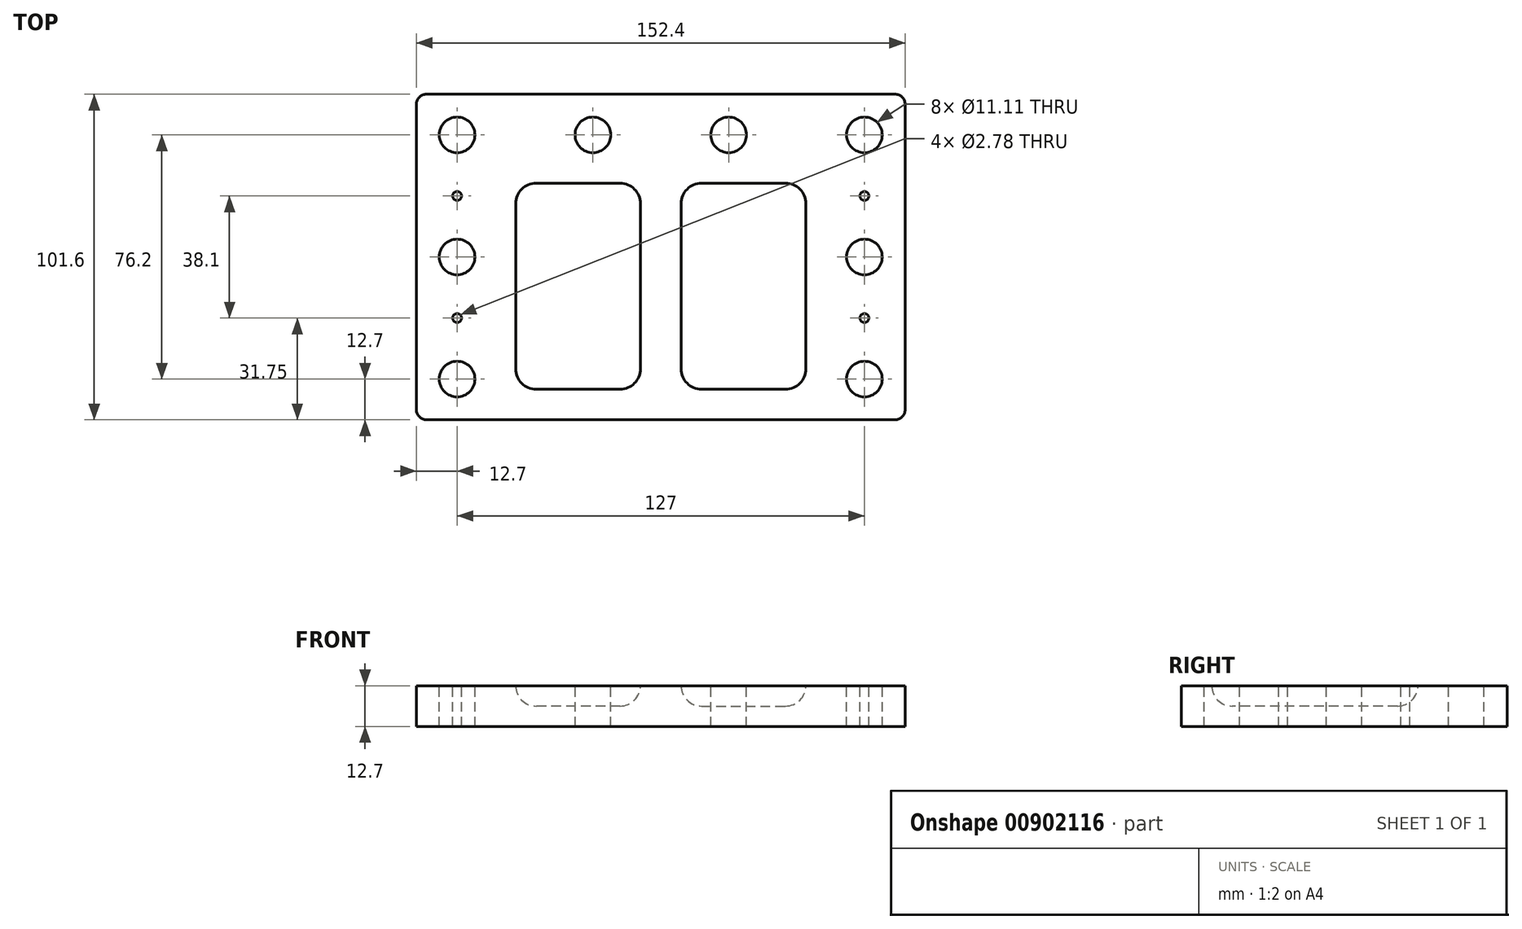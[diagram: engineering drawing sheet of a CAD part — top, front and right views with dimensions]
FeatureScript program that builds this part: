
annotation { "Feature Type Name" : "Feature", "Feature Type Description" : "" }
export const myFeature = defineFeature(function(context is Context, id is Id, definition is map)
    precondition{}
    {
        {
            var Q0;
            Q0=qCreatedBy(makeId("Top.planeOp"),FACE);
            var sketch = newSketch(context, id + "F0", { "sketchPlane" : qUnion([Q0])});
            skLineSegment(sketch, "E0.bottom", {"start": v(73.03, -50.8) * mm, "end": v(-73.02, -50.8) * mm});
            skLineSegment(sketch, "E0.top", {"start": v(73.03, 50.8) * mm, "end": v(-73.02, 50.8) * mm});
            skLineSegment(sketch, "E0.left", {"start": v(76.2, -47.63) * mm, "end": v(76.2, 47.63) * mm});
            skLineSegment(sketch, "E0.right", {"start": v(-76.2, -47.63) * mm, "end": v(-76.2, 47.63) * mm});
            skPoint(sketch, "E0.middle", {"position": v(0, 0) * mm});
            skPoint(sketch, "E1.visualSharp", {"position": v(76.2, -50.8) * mm});
            skArc(sketch, "E1.filletArc", {"start": v(73.03, -50.8) * mm, "mid": v(75.27, -49.87) * mm, "end": v(76.2, -47.63) * mm});
            skPoint(sketch, "E2.visualSharp", {"position": v(76.2, 50.8) * mm});
            skArc(sketch, "E2.filletArc", {"start": v(76.2, 47.63) * mm, "mid": v(75.27, 49.87) * mm, "end": v(73.03, 50.8) * mm});
            skPoint(sketch, "E3.visualSharp", {"position": v(-76.2, 50.8) * mm});
            skArc(sketch, "E3.filletArc", {"start": v(-73.02, 50.8) * mm, "mid": v(-75.27, 49.87) * mm, "end": v(-76.2, 47.63) * mm});
            skPoint(sketch, "E4.visualSharp", {"position": v(-76.2, -50.8) * mm});
            skArc(sketch, "E4.filletArc", {"start": v(-76.2, -47.63) * mm, "mid": v(-75.27, -49.87) * mm, "end": v(-73.02, -50.8) * mm});
            skSolve(sketch);
        }
        {
            var Q0;
            Q0 = qSketchRegion(id + "F0", true);
            extrude(context, id + "F1", {"entities" : qUnion([Q0]), "depth" : 12.7 * mm, "offsetDistance" : 25.4 * mm});
        }
        {
            var Q0;
            Q0=makeQuery(id+"F1.opExtrude","CAP_FACE",FACE,{"disambiguationData":[OSD([sQuery(id+"F0.wireOp",EDGE,"E0.bottom"),sQuery(id+"F0.wireOp",EDGE,"E0.top"),sQuery(id+"F0.wireOp",EDGE,"E0.left"),sQuery(id+"F0.wireOp",EDGE,"E0.right"),sQuery(id+"F0.wireOp",EDGE,"E1.filletArc"),sQuery(id+"F0.wireOp",EDGE,"E2.filletArc"),sQuery(id+"F0.wireOp",EDGE,"E3.filletArc"),sQuery(id+"F0.wireOp",EDGE,"E4.filletArc")])],"isStart":false});
            var sketch = newSketch(context, id + "F2", { "sketchPlane" : qUnion([Q0])});
            skCircle(sketch, "E5", {"center": v(-63.5, -19.05) * mm, "radius": 1.39 * mm});
            skCircle(sketch, "E6", {"center": v(63.5, 19.05) * mm, "radius": 1.39 * mm});
            skCircle(sketch, "E7", {"center": v(63.5, -19.05) * mm, "radius": 1.39 * mm});
            skCircle(sketch, "E8", {"center": v(-63.5, 19.05) * mm, "radius": 1.39 * mm});
            skLineSegment(sketch, "E9", {"start": v(-63.5, 19.05) * mm, "end": v(63.5, -19.05) * mm, "construction": true});
            skLineSegment(sketch, "E10", {"start": v(-63.5, -19.05) * mm, "end": v(63.5, 19.05) * mm, "construction": true});
            skSolve(sketch);
        }
        {
            var Q0;
            Q0=makeQuery(id+"F1.opExtrude","CAP_FACE",FACE,{"disambiguationData":[OSD([sQuery(id+"F0.wireOp",EDGE,"E0.bottom"),sQuery(id+"F0.wireOp",EDGE,"E0.top"),sQuery(id+"F0.wireOp",EDGE,"E0.left"),sQuery(id+"F0.wireOp",EDGE,"E0.right"),sQuery(id+"F0.wireOp",EDGE,"E1.filletArc"),sQuery(id+"F0.wireOp",EDGE,"E2.filletArc"),sQuery(id+"F0.wireOp",EDGE,"E3.filletArc"),sQuery(id+"F0.wireOp",EDGE,"E4.filletArc")])],"isStart":false});
            var sketch = newSketch(context, id + "F3", { "sketchPlane" : qUnion([Q0])});
            skCircle(sketch, "E11", {"center": v(-63.5, 38.1) * mm, "radius": 5.56 * mm});
            skCircle(sketch, "E12", {"center": v(63.5, 38.1) * mm, "radius": 5.56 * mm});
            skCircle(sketch, "E13", {"center": v(63.5, -38.1) * mm, "radius": 5.56 * mm});
            skCircle(sketch, "E14", {"center": v(-63.5, -38.1) * mm, "radius": 5.56 * mm});
            skCircle(sketch, "E15", {"center": v(-63.5, 0) * mm, "radius": 5.56 * mm});
            skCircle(sketch, "E16", {"center": v(63.5, 0) * mm, "radius": 5.56 * mm});
            skCircle(sketch, "E17", {"center": v(-21.17, 38.1) * mm, "radius": 5.56 * mm});
            skCircle(sketch, "E18", {"center": v(21.17, 38.1) * mm, "radius": 5.56 * mm});
            skLineSegment(sketch, "E19", {"start": v(-63.5, 38.1) * mm, "end": v(-63.5, 0) * mm, "construction": true});
            skLineSegment(sketch, "E20", {"start": v(-63.5, 0) * mm, "end": v(-63.5, -38.1) * mm, "construction": true});
            skLineSegment(sketch, "E21", {"start": v(63.5, 38.1) * mm, "end": v(21.17, 38.1) * mm, "construction": true});
            skLineSegment(sketch, "E22", {"start": v(-63.5, 38.1) * mm, "end": v(-21.17, 38.1) * mm, "construction": true});
            skLineSegment(sketch, "E23", {"start": v(-21.17, 38.1) * mm, "end": v(21.17, 38.1) * mm, "construction": true});
            skSolve(sketch);
        }
        {
            var Q0;
            Q0 = qSketchRegion(id + "F3", true);
            extrude(context, id + "F4", {"entities" : qUnion([Q0]), "operationType" : NewBodyOperationType.REMOVE, "endBound" : BoundingType.THROUGH_ALL, "oppositeDirection" : true, "depth" : 25.4 * mm, "offsetDistance" : 25.4 * mm});
        }
        {
            var Q0;
            Q0 = qSketchRegion(id + "F2", true);
            extrude(context, id + "F5", {"entities" : qUnion([Q0]), "operationType" : NewBodyOperationType.REMOVE, "endBound" : BoundingType.THROUGH_ALL, "oppositeDirection" : true, "depth" : 25.4 * mm, "offsetDistance" : 25.4 * mm});
        }
        {
            var Q0;
            Q0=makeQuery(id+"F1.opExtrude","CAP_FACE",FACE,{"disambiguationData":[OSD([sQuery(id+"F0.wireOp",EDGE,"E0.bottom"),sQuery(id+"F0.wireOp",EDGE,"E0.top"),sQuery(id+"F0.wireOp",EDGE,"E0.left"),sQuery(id+"F0.wireOp",EDGE,"E0.right"),sQuery(id+"F0.wireOp",EDGE,"E1.filletArc"),sQuery(id+"F0.wireOp",EDGE,"E2.filletArc"),sQuery(id+"F0.wireOp",EDGE,"E3.filletArc"),sQuery(id+"F0.wireOp",EDGE,"E4.filletArc")])],"isStart":false});
            var sketch = newSketch(context, id + "F6", { "sketchPlane" : qUnion([Q0])});
            skLineSegment(sketch, "E24.bottom", {"start": v(-12.7, 23.02) * mm, "end": v(-38.9, 23.02) * mm});
            skLineSegment(sketch, "E24.top", {"start": v(-12.7, -41.28) * mm, "end": v(-38.9, -41.28) * mm});
            skLineSegment(sketch, "E24.left", {"start": v(-6.35, 16.67) * mm, "end": v(-6.35, -34.93) * mm});
            skLineSegment(sketch, "E24.right", {"start": v(-45.24, 16.67) * mm, "end": v(-45.24, -34.93) * mm});
            skPoint(sketch, "E24.middle", {"position": v(-25.8, -9.13) * mm});
            skPoint(sketch, "E25.visualSharp", {"position": v(-6.35, 23.02) * mm});
            skArc(sketch, "E25.filletArc", {"start": v(-6.35, 16.67) * mm, "mid": v(-8.2, 21.16) * mm, "end": v(-12.7, 23.02) * mm});
            skPoint(sketch, "E26.visualSharp", {"position": v(-45.24, 23.02) * mm});
            skArc(sketch, "E26.filletArc", {"start": v(-38.9, 23.02) * mm, "mid": v(-43.38, 21.16) * mm, "end": v(-45.24, 16.67) * mm});
            skPoint(sketch, "E27.visualSharp", {"position": v(-45.24, -41.28) * mm});
            skArc(sketch, "E27.filletArc", {"start": v(-45.24, -34.93) * mm, "mid": v(-43.38, -39.42) * mm, "end": v(-38.9, -41.28) * mm});
            skPoint(sketch, "E28.visualSharp", {"position": v(-6.35, -41.28) * mm});
            skArc(sketch, "E28.filletArc", {"start": v(-12.7, -41.28) * mm, "mid": v(-8.2, -39.42) * mm, "end": v(-6.35, -34.93) * mm});
            skArc(sketch, "E29.MirrorCS", {"start": v(12.7, -41.28) * mm, "mid": v(8.2, -39.42) * mm, "end": v(6.35, -34.93) * mm});
            skArc(sketch, "E30.MirrorCS", {"start": v(45.24, -34.93) * mm, "mid": v(43.38, -39.42) * mm, "end": v(38.9, -41.28) * mm});
            skArc(sketch, "E31.MirrorCS", {"start": v(38.9, 23.02) * mm, "mid": v(43.38, 21.16) * mm, "end": v(45.24, 16.67) * mm});
            skArc(sketch, "E32.MirrorCS", {"start": v(6.35, 16.67) * mm, "mid": v(8.2, 21.16) * mm, "end": v(12.7, 23.02) * mm});
            skLineSegment(sketch, "E33.MirrorCS", {"start": v(45.24, 16.67) * mm, "end": v(45.24, -34.93) * mm});
            skPoint(sketch, "E34.MirrorP", {"position": v(6.35, 23.02) * mm});
            skPoint(sketch, "E35.MirrorP", {"position": v(25.8, -9.13) * mm});
            skLineSegment(sketch, "E36.MirrorCS", {"start": v(12.7, 23.02) * mm, "end": v(38.9, 23.02) * mm});
            skPoint(sketch, "E37.MirrorP", {"position": v(45.24, -41.28) * mm});
            skPoint(sketch, "E38.MirrorP", {"position": v(6.35, -41.28) * mm});
            skPoint(sketch, "E39.MirrorP", {"position": v(45.24, 23.02) * mm});
            skLineSegment(sketch, "E40.MirrorCS", {"start": v(6.35, 16.67) * mm, "end": v(6.35, -34.93) * mm});
            skLineSegment(sketch, "E41.MirrorCS", {"start": v(12.7, -41.28) * mm, "end": v(38.9, -41.28) * mm});
            skSolve(sketch);
        }
        {
            var Q0;
            Q0 = qSketchRegion(id + "F6", true);
            extrude(context, id + "F7", {"entities" : qUnion([Q0]), "operationType" : NewBodyOperationType.REMOVE, "oppositeDirection" : true, "depth" : 6.35 * mm, "offsetDistance" : 25.4 * mm});
        }
        {
            var Q0;
            Q0=makeQuery(id+"F7.boolean.opBoolean","COPY",EDGE,{"derivedFrom":makeQuery(id+"F7.opExtrude","CAP_EDGE",EDGE,{"disambiguationData":[OSD([sQuery(id+"F6.wireOp",EDGE,"E24.top")])],"isStart":false})});
            var Q1;
            Q1=makeQuery(id+"F7.boolean.opBoolean","COPY",EDGE,{"derivedFrom":makeQuery(id+"F7.opExtrude","CAP_EDGE",EDGE,{"disambiguationData":[OSD([sQuery(id+"F6.wireOp",EDGE,"E24.left")])],"isStart":false})});
            var Q2;
            Q2=makeQuery(id+"F7.boolean.opBoolean","COPY",EDGE,{"derivedFrom":makeQuery(id+"F7.opExtrude","CAP_EDGE",EDGE,{"disambiguationData":[OSD([sQuery(id+"F6.wireOp",EDGE,"E28.filletArc")])],"isStart":false})});
            var Q3;
            Q3=makeQuery(id+"F7.boolean.opBoolean","COPY",EDGE,{"derivedFrom":makeQuery(id+"F7.opExtrude","CAP_EDGE",EDGE,{"disambiguationData":[OSD([sQuery(id+"F6.wireOp",EDGE,"E24.right")])],"isStart":false})});
            var Q4;
            Q4=makeQuery(id+"F7.boolean.opBoolean","COPY",EDGE,{"derivedFrom":makeQuery(id+"F7.opExtrude","CAP_EDGE",EDGE,{"disambiguationData":[OSD([sQuery(id+"F6.wireOp",EDGE,"E27.filletArc")])],"isStart":false})});
            var Q5;
            Q5=makeQuery(id+"F7.boolean.opBoolean","COPY",EDGE,{"derivedFrom":makeQuery(id+"F7.opExtrude","CAP_EDGE",EDGE,{"disambiguationData":[OSD([sQuery(id+"F6.wireOp",EDGE,"E26.filletArc")])],"isStart":false})});
            var Q6;
            Q6=makeQuery(id+"F7.boolean.opBoolean","COPY",EDGE,{"derivedFrom":makeQuery(id+"F7.opExtrude","CAP_EDGE",EDGE,{"disambiguationData":[OSD([sQuery(id+"F6.wireOp",EDGE,"E24.bottom")])],"isStart":false})});
            var Q7;
            Q7=makeQuery(id+"F7.boolean.opBoolean","COPY",EDGE,{"derivedFrom":makeQuery(id+"F7.opExtrude","CAP_EDGE",EDGE,{"disambiguationData":[OSD([sQuery(id+"F6.wireOp",EDGE,"E25.filletArc")])],"isStart":false})});
            fillet(context, id + "F8", {"entities" : qUnion([Q0, Q1, Q2, Q3, Q4, Q5, Q6, Q7]), "radius" : 6.35 * mm, "tangentPropagation" : true, "allowEdgeOverflow" : false});
        }
        {
            var Q0;
            Q0=makeQuery(id+"F7.boolean.opBoolean","COPY",EDGE,{"derivedFrom":makeQuery(id+"F7.opExtrude","CAP_EDGE",EDGE,{"disambiguationData":[OSD([sQuery(id+"F6.wireOp",EDGE,"E40.MirrorCS")])],"isStart":false})});
            var Q1;
            Q1=makeQuery(id+"F7.boolean.opBoolean","COPY",EDGE,{"derivedFrom":makeQuery(id+"F7.opExtrude","CAP_EDGE",EDGE,{"disambiguationData":[OSD([sQuery(id+"F6.wireOp",EDGE,"E32.MirrorCS")])],"isStart":false})});
            var Q2;
            Q2=makeQuery(id+"F7.boolean.opBoolean","COPY",EDGE,{"derivedFrom":makeQuery(id+"F7.opExtrude","CAP_EDGE",EDGE,{"disambiguationData":[OSD([sQuery(id+"F6.wireOp",EDGE,"E36.MirrorCS")])],"isStart":false})});
            var Q3;
            Q3=makeQuery(id+"F7.boolean.opBoolean","COPY",EDGE,{"derivedFrom":makeQuery(id+"F7.opExtrude","CAP_EDGE",EDGE,{"disambiguationData":[OSD([sQuery(id+"F6.wireOp",EDGE,"E31.MirrorCS")])],"isStart":false})});
            var Q4;
            Q4=makeQuery(id+"F7.boolean.opBoolean","COPY",EDGE,{"derivedFrom":makeQuery(id+"F7.opExtrude","CAP_EDGE",EDGE,{"disambiguationData":[OSD([sQuery(id+"F6.wireOp",EDGE,"E33.MirrorCS")])],"isStart":false})});
            var Q5;
            Q5=makeQuery(id+"F7.boolean.opBoolean","COPY",EDGE,{"derivedFrom":makeQuery(id+"F7.opExtrude","CAP_EDGE",EDGE,{"disambiguationData":[OSD([sQuery(id+"F6.wireOp",EDGE,"E30.MirrorCS")])],"isStart":false})});
            var Q6;
            Q6=makeQuery(id+"F7.boolean.opBoolean","COPY",EDGE,{"derivedFrom":makeQuery(id+"F7.opExtrude","CAP_EDGE",EDGE,{"disambiguationData":[OSD([sQuery(id+"F6.wireOp",EDGE,"E41.MirrorCS")])],"isStart":false})});
            var Q7;
            Q7=makeQuery(id+"F7.boolean.opBoolean","COPY",EDGE,{"derivedFrom":makeQuery(id+"F7.opExtrude","CAP_EDGE",EDGE,{"disambiguationData":[OSD([sQuery(id+"F6.wireOp",EDGE,"E29.MirrorCS")])],"isStart":false})});
            fillet(context, id + "F9", {"entities" : qUnion([Q0, Q1, Q2, Q3, Q4, Q5, Q6, Q7]), "radius" : 6.35 * mm, "tangentPropagation" : true, "allowEdgeOverflow" : false});
        }
    });
